# Revit family: ASH_ArmitageShanks_Urinals_Contour_S611001 (ASH_Contour21_S6110_BIM_GB)
name_source: partatom
category: Plumbing Fixtures
revit_build: Autodesk Revit MEP 2012 (Build: 20110309_2315(x64)
units: mm (PartAtom-declared; Revit-internal decimal feet)

## types (1)
- S611001 - Contour Urinal 67cm Back Inlet Concealed
    AreaUnits = millimeters
    Assembly Code = C1030200
    AssetType = Fixed
    BIMObjectName = ASH_ArmitageShanks_WallHungUrinals_Contour_S6110
    Brand = Armitage Shanks
    CWFU = 0
    ConnectionType = PLUMBING
    Default Elevation = 610 mm  [stored 2.00131 ft]
    Description = Contour urinal 67 cm back inlet concealed
    DurationUnit = year
    ECA = No
    ExpectedLife = 30
    Features = Urinal 67 cm back inlet concealed
    Finish = White
    HWFU = 0
    IfcExportAs = IfcSanitaryTerminalType
    IfcExportType = URINAL
    LinearUnits = millimeters
    ManufacturerURL = www.idealspec.co.uk
    Model = S611001
    ModelNumber = S611001
    ModelReference = Contour urinal 67 cm back inlet concealed
    NBSDescription = Wall hung urinals
    NBSReference = 45-35-70/350
    Name = WallHungUrinals_Contour_S6110_ArmitageShanks
    NettWeight = 16 Kg
    NominalDepth = 305 mm
    NominalHeight = 675 mm  [stored 2.21457 ft]
    NominalLength = 305 mm
    NominalWidth = 400 mm  [stored 1.31234 ft]
    ProductInformation = www.idealspec.co.uk/datasheets/S611001
    Shape = Rectangular
    Size = 675 x 305 x 400 mm
    Space = Internal
    SpilloverLevel = 0 mm  [stored 0 ft]
    URL = www.idealspec.co.uk
    Uniclass2 = Pr_40_20_93_82
    UrinalColor = White
    UrinalMaterial = Vitreous china
    UrinalType = Bowl
    Version = 2
    VolumeUnits = Litres
    WFU = 0
    WRAS = No
    WarrantyDescription = Manufacturers warranty
    WarrantyDurationParts = 99
    WarrantyDurationUnit = year
    WaterEfficientProduct = No

note: [stored X ft] marks values corroborated as IEEE doubles in the binary element streams (Revit-internal decimal feet)

## geometry (parser evidence)
native form markers: Blend x2, Sweep x2
no freeform markers — native parametric forms only
